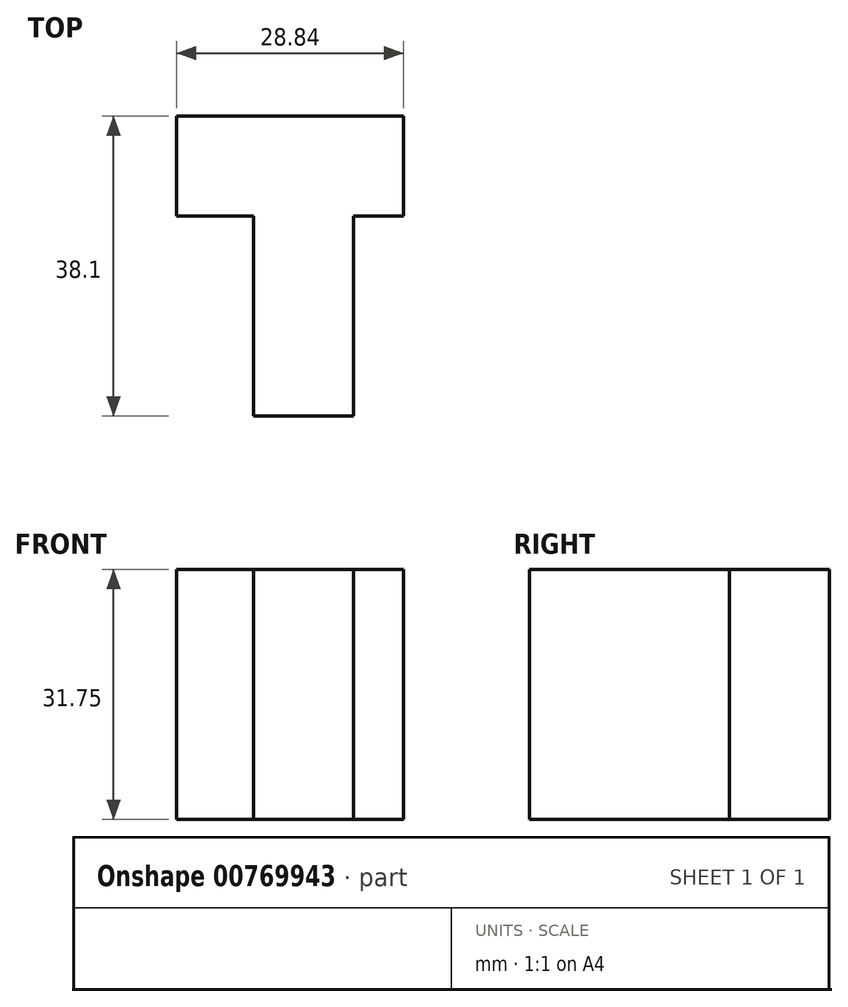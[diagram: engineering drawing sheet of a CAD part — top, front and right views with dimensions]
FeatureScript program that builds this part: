
annotation { "Feature Type Name" : "Feature", "Feature Type Description" : "" }
export const myFeature = defineFeature(function(context is Context, id is Id, definition is map)
    precondition{}
    {
        {
            var Q0;
            Q0=qCreatedBy(makeId("Top.planeOp"),FACE);
            var sketch = newSketch(context, id + "F0", { "sketchPlane" : qUnion([Q0])});
            skLineSegment(sketch, "E0", {"start": v(0, 0) * mm, "end": v(12.7, 0) * mm});
            skLineSegment(sketch, "E1", {"start": v(12.7, 0) * mm, "end": v(12.7, 25.4) * mm});
            skLineSegment(sketch, "E2", {"start": v(12.7, 25.4) * mm, "end": v(19.05, 25.4) * mm});
            skLineSegment(sketch, "E3", {"start": v(19.05, 25.4) * mm, "end": v(19.05, 38.1) * mm});
            skLineSegment(sketch, "E4", {"start": v(19.05, 38.1) * mm, "end": v(-9.79, 38.1) * mm});
            skLineSegment(sketch, "E5", {"start": v(-9.79, 38.1) * mm, "end": v(-9.79, 25.4) * mm});
            skLineSegment(sketch, "E6", {"start": v(-9.79, 25.4) * mm, "end": v(0, 25.4) * mm});
            skLineSegment(sketch, "E7", {"start": v(0, 25.4) * mm, "end": v(0, 0) * mm});
            skSolve(sketch);
        }
        {
            var Q0;
            Q0 = qSketchRegion(id + "F0", true);
            extrude(context, id + "F1", {"entities" : qUnion([Q0]), "depth" : 31.75 * mm, "offsetDistance" : 25.4 * mm});
        }
    });
